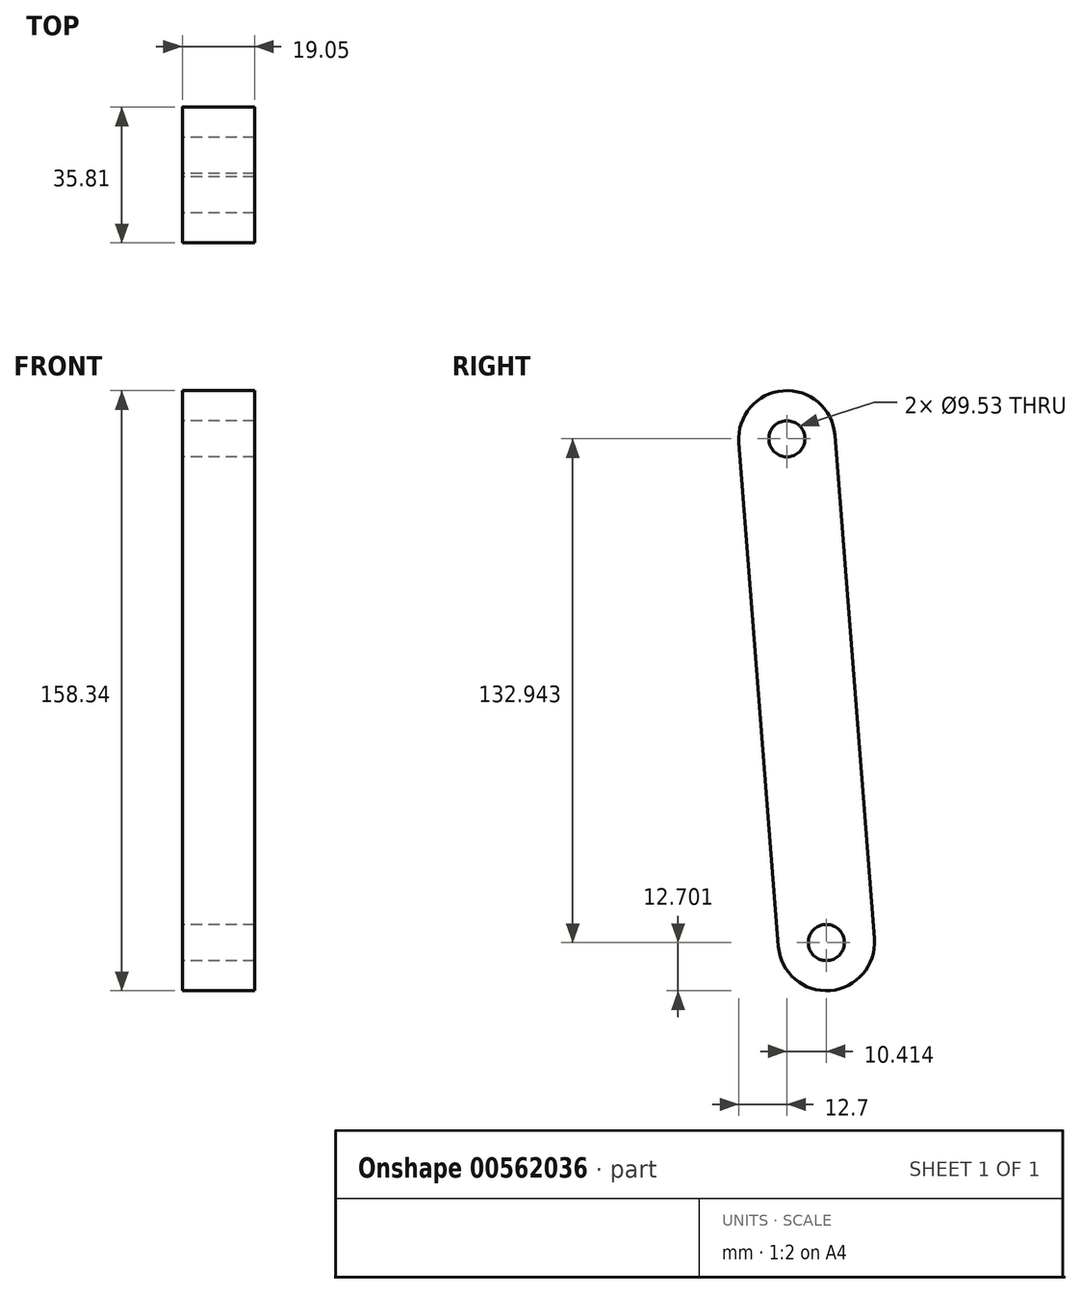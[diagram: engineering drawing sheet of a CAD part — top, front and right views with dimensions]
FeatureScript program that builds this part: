
annotation { "Feature Type Name" : "Feature", "Feature Type Description" : "" }
export const myFeature = defineFeature(function(context is Context, id is Id, definition is map)
    precondition{}
    {
        {
            var Q0;
            Q0=qCreatedBy(makeId("Right.planeOp"),FACE);
            var sketch = newSketch(context, id + "F0", { "sketchPlane" : qUnion([Q0])});
            skLineSegment(sketch, "E0", {"start": v(-513.86, 319.86) * mm, "end": v(-513.86, 78.56) * mm});
            skSolve(sketch);
        }
        {
            var Q0;
            Q0=qCreatedBy(makeId("Right.planeOp"),FACE);
            var sketch = newSketch(context, id + "F1", { "sketchPlane" : qUnion([Q0])});
            skLineSegment(sketch, "E1", {"start": v(-749.75, 255.82) * mm, "end": v(-601.81, 261.03) * mm});
            skLineSegment(sketch, "E2", {"start": v(-562.01, 653.81) * mm, "end": v(-601.81, 261.03) * mm});
            skLineSegment(sketch, "E3", {"start": v(-562.01, 653.81) * mm, "end": v(-749.75, 255.82) * mm});
            skLineSegment(sketch, "E4", {"start": v(-712.77, 291.22) * mm, "end": v(-724.6, 436.35) * mm});
            skLineSegment(sketch, "E5", {"start": v(-712.77, 291.22) * mm, "end": v(-827.72, 541.93) * mm});
            skLineSegment(sketch, "E6", {"start": v(-724.6, 436.35) * mm, "end": v(-827.72, 541.93) * mm});
            skLineSegment(sketch, "E7", {"start": v(-1010.22, 658.42) * mm, "end": v(-827.72, 541.93) * mm});
            skLineSegment(sketch, "E8", {"start": v(-1039.51, 675.34) * mm, "end": v(-1010.22, 658.42) * mm});
            skLineSegment(sketch, "E9", {"start": v(-1039.51, 675.34) * mm, "end": v(-712.77, 291.22) * mm});
            skLineSegment(sketch, "E10", {"start": v(-1010.22, 658.42) * mm, "end": v(-712.77, 291.22) * mm});
            skLineSegment(sketch, "E11", {"start": v(-601.81, 261.03) * mm, "end": v(-595.89, 401.8) * mm});
            skLineSegment(sketch, "E12", {"start": v(-601.81, 261.03) * mm, "end": v(-609.7, 655.84) * mm});
            skLineSegment(sketch, "E13", {"start": v(-595.89, 401.8) * mm, "end": v(-609.7, 655.84) * mm});
            skLineSegment(sketch, "E14", {"start": v(-724.6, 436.35) * mm, "end": v(-595.89, 401.8) * mm});
            skLineSegment(sketch, "E15", {"start": v(-827.72, 541.93) * mm, "end": v(-776.2, 589.57) * mm});
            skLineSegment(sketch, "E16", {"start": v(-749.75, 255.82) * mm, "end": v(-776.2, 589.57) * mm});
            skLineSegment(sketch, "E17", {"start": v(-1043.9, 791.38) * mm, "end": v(-776.2, 589.57) * mm});
            skLineSegment(sketch, "E18", {"start": v(-1392.46, 315.43) * mm, "end": v(-1338.48, 358.4) * mm});
            skLineSegment(sketch, "E19", {"start": v(-1338.48, 358.4) * mm, "end": v(-1296.78, 299.05) * mm});
            skLineSegment(sketch, "E20", {"start": v(-1043.9, 791.38) * mm, "end": v(-1296.78, 299.05) * mm});
            skLineSegment(sketch, "E21", {"start": v(-1296.78, 299.05) * mm, "end": v(-1039.51, 675.34) * mm});
            skLineSegment(sketch, "E22", {"start": v(-1039.51, 675.34) * mm, "end": v(-1043.9, 791.38) * mm});
            skLineSegment(sketch, "E23", {"start": v(-1010.22, 658.42) * mm, "end": v(-1338.48, 358.4) * mm});
            skLineSegment(sketch, "E24", {"start": v(-1392.46, 315.43) * mm, "end": v(-1296.78, 299.05) * mm});
            skLineSegment(sketch, "E25", {"start": v(-1296.78, 299.05) * mm, "end": v(-1296.78, 190.05) * mm});
            skLineSegment(sketch, "E26", {"start": v(-1296.78, 190.05) * mm, "end": v(-1404.89, 208.55) * mm});
            skLineSegment(sketch, "E27", {"start": v(-1404.89, 208.55) * mm, "end": v(-1392.46, 315.43) * mm});
            skLineSegment(sketch, "E28", {"start": v(-1392.46, 315.43) * mm, "end": v(-1296.78, 190.05) * mm});
            skLineSegment(sketch, "E29", {"start": v(0, 0) * mm, "end": v(0, 674.17) * mm});
            skLineSegment(sketch, "E30", {"start": v(-316.61, 320.6) * mm, "end": v(-316.61, 307.94) * mm});
            skLineSegment(sketch, "E31", {"start": v(-400.45, 218.07) * mm, "end": v(-378.01, 218.07) * mm});
            skLineSegment(sketch, "E32", {"start": v(-472.6, 74.76) * mm, "end": v(-472.6, 54.94) * mm});
            skSolve(sketch);
        }
        {
            var Q0;
            Q0=qCreatedBy(makeId("Right.planeOp"),FACE);
            var sketch = newSketch(context, id + "F2", { "sketchPlane" : qUnion([Q0])});
            skArc(sketch, "E33", {"start": v(-772.82, 387.77) * mm, "mid": v(-761.15, 401.42) * mm, "end": v(-747.5, 389.76) * mm});
            skArc(sketch, "E34", {"start": v(-762.4, 254.83) * mm, "mid": v(-748.75, 243.16) * mm, "end": v(-737.08, 256.81) * mm});
            skLineSegment(sketch, "E35", {"start": v(-762.4, 254.83) * mm, "end": v(-772.82, 387.77) * mm});
            skLineSegment(sketch, "E36", {"start": v(-747.5, 389.76) * mm, "end": v(-737.08, 256.81) * mm});
            skCircle(sketch, "E37", {"center": v(-760.16, 388.76) * mm, "radius": 4.76 * mm});
            skCircle(sketch, "E38", {"center": v(-749.75, 255.82) * mm, "radius": 4.76 * mm});
            skSolve(sketch);
        }
        {
            var Q0;
            Q0=qSketchRegion(id+"F2",true);
            extrude(context, id + "F3", {"entities" : qUnion([Q0]), "depth" : 19.05 * mm, "offsetDistance" : 25.4 * mm});
        }
    });
